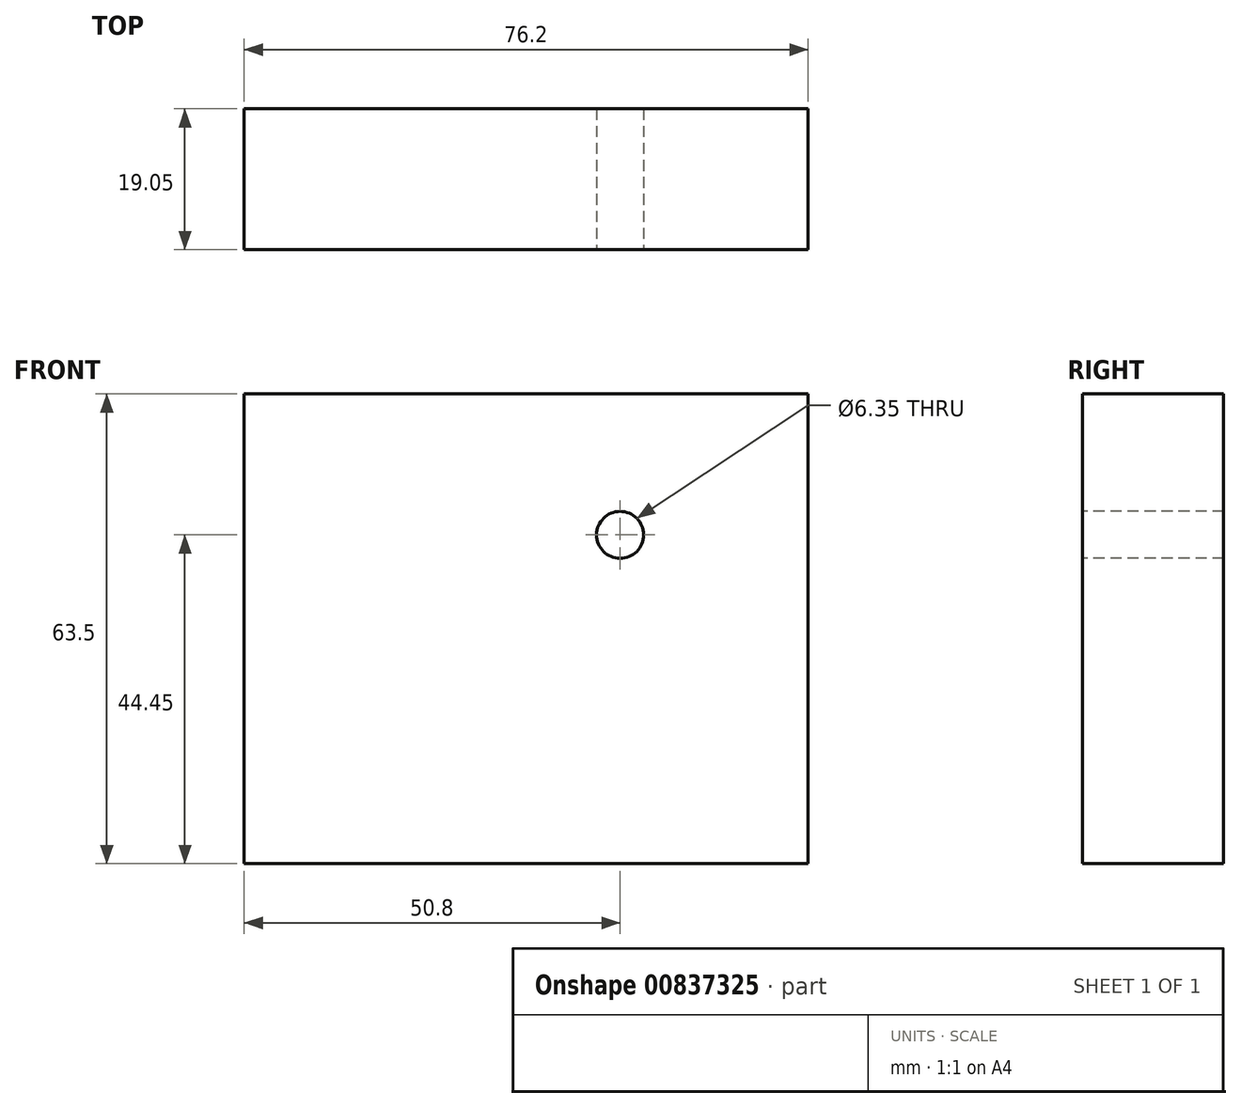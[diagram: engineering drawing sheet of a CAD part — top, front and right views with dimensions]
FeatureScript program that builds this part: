
annotation { "Feature Type Name" : "Feature", "Feature Type Description" : "" }
export const myFeature = defineFeature(function(context is Context, id is Id, definition is map)
    precondition{}
    {
        {
            var Q0;
            Q0=qCreatedBy(makeId("Front.planeOp"),FACE);
            var sketch = newSketch(context, id + "F0", { "sketchPlane" : qUnion([Q0])});
            skLineSegment(sketch, "E0.bottom", {"start": v(0, 0) * mm, "end": v(76.2, 0) * mm});
            skLineSegment(sketch, "E0.top", {"start": v(0, 63.5) * mm, "end": v(76.2, 63.5) * mm});
            skLineSegment(sketch, "E0.left", {"start": v(0, 0) * mm, "end": v(0, 63.5) * mm});
            skLineSegment(sketch, "E0.right", {"start": v(76.2, 0) * mm, "end": v(76.2, 63.5) * mm});
            skSolve(sketch);
        }
        {
            var Q0;
            Q0=makeQuery(id+"F0.imprint","IMPRINT",FACE,{"disambiguationData":[TD([[makeQuery(id+"F0.imprint","IMPRINT",EDGE,{"derivedFrom":sQuery(id+"F0.wireOp",EDGE,"E0.bottom")}),1.0]])]});
            extrude(context, id + "F1", {"entities" : qUnion([Q0]), "depth" : 19.05 * mm, "offsetDistance" : 25.4 * mm});
        }
        {
            var Q0;
            Q0=makeQuery(id+"F1.opExtrude","CAP_FACE",FACE,{"disambiguationData":[OSD([sQuery(id+"F0.wireOp",EDGE,"E0.bottom"),sQuery(id+"F0.wireOp",EDGE,"E0.top"),sQuery(id+"F0.wireOp",EDGE,"E0.left"),sQuery(id+"F0.wireOp",EDGE,"E0.right")])],"isStart":false});
            var sketch = newSketch(context, id + "F2", { "sketchPlane" : qUnion([Q0])});
            skLineSegment(sketch, "E1", {"start": v(0, 44.45) * mm, "end": v(76.2, 44.45) * mm, "construction": true});
            skPoint(sketch, "E2", {"position": v(50.8, 44.45) * mm});
            skSolve(sketch);
        }
        {
            var Q0;
            Q0=sQuery(id+"F2.wireOp",VERTEX,"E2");
            var Q1;
            Q1=makeQuery(id+"F1.opExtrude","SWEPT_BODY",BODY,{"disambiguationData":[OSD([sQuery(id+"F0.wireOp",EDGE,"E0.bottom"),sQuery(id+"F0.wireOp",EDGE,"E0.top"),sQuery(id+"F0.wireOp",EDGE,"E0.left"),sQuery(id+"F0.wireOp",EDGE,"E0.right")])]});
            hole(context, id + "F3", {"style" : HoleStyle.SIMPLE, "endStyle" : HoleEndStyle.THROUGH, "holeDiameter" : 6.35 * mm, "majorDiameter" : 6.35 * mm, "isTappedThrough" : true, "tappedDepth" : 12.7 * mm, "tapClearance" : 3, "locations" : qUnion([Q0]), "scope" : qUnion([Q1])});
        }
    });
